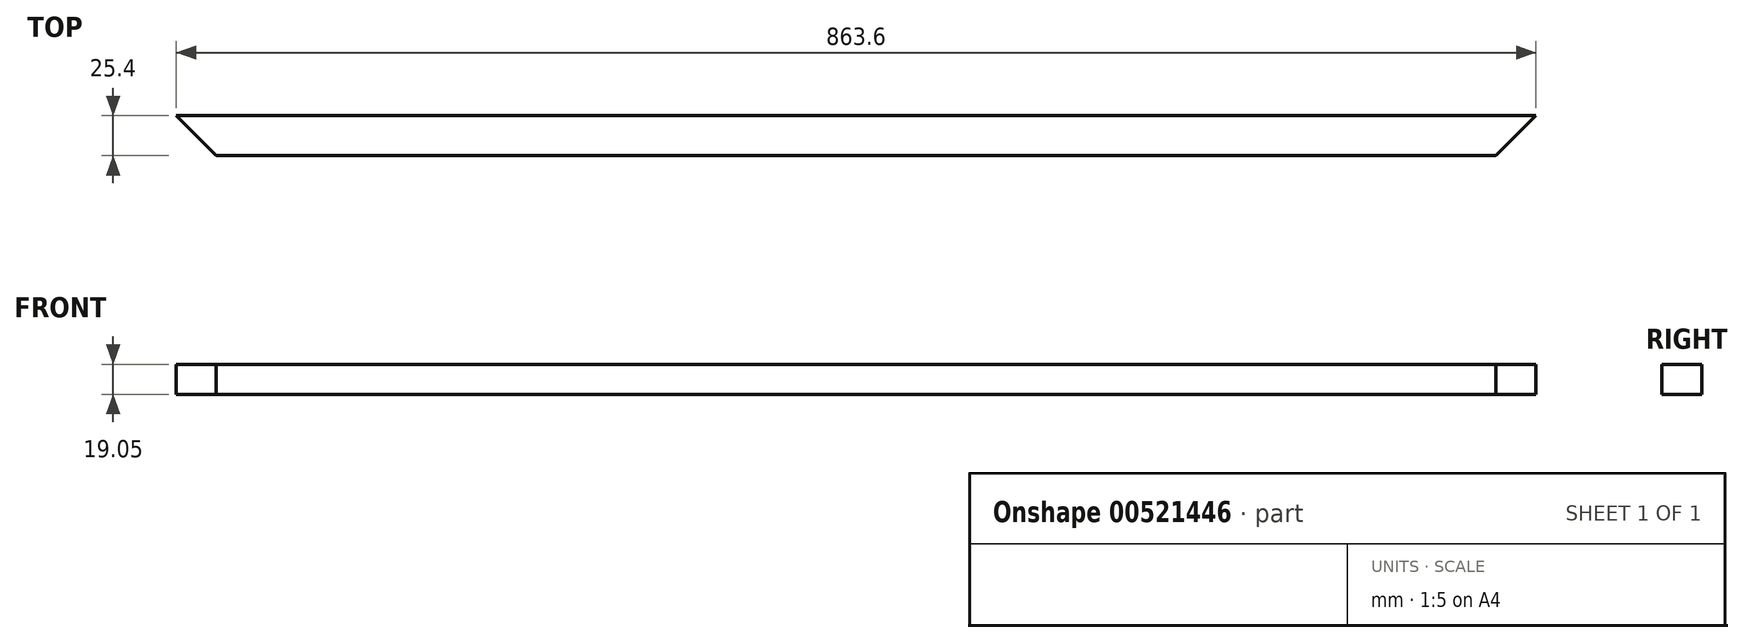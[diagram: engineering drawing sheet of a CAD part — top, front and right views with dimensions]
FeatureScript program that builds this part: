
annotation { "Feature Type Name" : "Feature", "Feature Type Description" : "" }
export const myFeature = defineFeature(function(context is Context, id is Id, definition is map)
    precondition{}
    {
        {
            var Q0;
            Q0=qCreatedBy(makeId("Top.planeOp"),FACE);
            var sketch = newSketch(context, id + "F0", { "sketchPlane" : qUnion([Q0])});
            skLineSegment(sketch, "E0.bottom", {"start": v(-420.8, -121.62) * mm, "end": v(442.8, -121.62) * mm});
            skLineSegment(sketch, "E0.top", {"start": v(-420.8, -147.02) * mm, "end": v(442.8, -147.02) * mm});
            skLineSegment(sketch, "E0.left", {"start": v(-420.8, -121.62) * mm, "end": v(-420.8, -147.02) * mm});
            skLineSegment(sketch, "E0.right", {"start": v(442.8, -121.62) * mm, "end": v(442.8, -147.02) * mm});
            skSolve(sketch);
        }
        {
            var Q0;
            Q0=makeQuery(id+"F0.imprint","IMPRINT",FACE,{"disambiguationData":[TD([[makeQuery(id+"F0.imprint","IMPRINT",EDGE,{"derivedFrom":sQuery(id+"F0.wireOp",EDGE,"E0.bottom")}),-1.0]])]});
            extrude(context, id + "F1", {"entities" : qUnion([Q0]), "depth" : 19.05 * mm, "offsetDistance" : 25.4 * mm});
        }
        {
            var Q0;
            Q0=makeQuery(id+"F1.opExtrude","SWEPT_EDGE",EDGE,{"disambiguationData":[OSD([sQuery(id+"F0.wireOp",EDGE,"E0.top"),sQuery(id+"F0.wireOp",EDGE,"E0.right")])]});
            var Q1;
            Q1=makeQuery(id+"F1.opExtrude","SWEPT_EDGE",EDGE,{"disambiguationData":[OSD([sQuery(id+"F0.wireOp",EDGE,"E0.top"),sQuery(id+"F0.wireOp",EDGE,"E0.left")])]});
            chamfer(context, id + "F2", {"entities" : qUnion([Q0, Q1]), "width" : 25.4 * mm, "tangentPropagation" : true});
        }
    });
